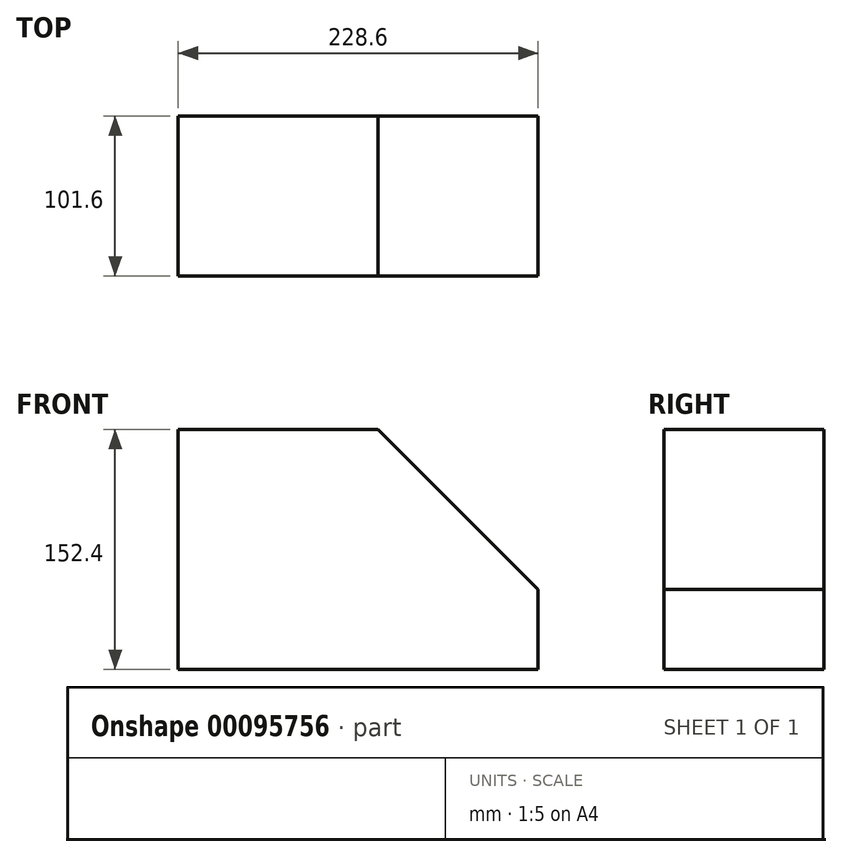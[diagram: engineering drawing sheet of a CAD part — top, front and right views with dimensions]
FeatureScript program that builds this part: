
annotation { "Feature Type Name" : "Feature", "Feature Type Description" : "" }
export const myFeature = defineFeature(function(context is Context, id is Id, definition is map)
    precondition{}
    {
        {
            var Q0;
            Q0=qCreatedBy(makeId("Front.planeOp"),FACE);
            var sketch = newSketch(context, id + "F0", { "sketchPlane" : qUnion([Q0])});
            skLineSegment(sketch, "E0.bottom", {"start": v(-74.7, 96.7) * mm, "end": v(52.3, 96.7) * mm});
            skLineSegment(sketch, "E0.top", {"start": v(-74.7, -55.7) * mm, "end": v(52.3, -55.7) * mm});
            skLineSegment(sketch, "E0.left", {"start": v(-74.7, 96.7) * mm, "end": v(-74.7, -55.7) * mm});
            skLineSegment(sketch, "E0.right", {"start": v(52.3, 96.7) * mm, "end": v(52.3, -55.7) * mm});
            skLineSegment(sketch, "E1", {"start": v(52.3, -55.7) * mm, "end": v(153.9, -55.7) * mm});
            skLineSegment(sketch, "E2", {"start": v(153.9, -55.7) * mm, "end": v(153.9, -4.9) * mm});
            skLineSegment(sketch, "E3", {"start": v(153.9, -4.9) * mm, "end": v(52.3, -4.9) * mm});
            skLineSegment(sketch, "E4", {"start": v(52.3, 96.7) * mm, "end": v(153.9, -4.9) * mm});
            skSolve(sketch);
        }
        {
            var Q0;
            Q0 = qSketchRegion(id + "F0", true);
            extrude(context, id + "F1", {"entities" : qUnion([Q0]), "depth" : 101.6 * mm});
        }
    });
